# Revit family: ARKOSLIGHT_Alaska Trimless
name_source: partatom
category: Lighting Fixtures
units: mm (PartAtom-declared; Revit-internal decimal feet)

## family parameters
Cut with Voids When Loaded = No
Host = Face
Light Source = No
Part Type = Normal
Room Calculation Point = No
Round Connector Dimension = Use Diameter
Shared = No

## types (2) — shared parameters
ARKOSLIGHT_Apparent Load = 5 VA
ARKOSLIGHT_Beam Angle = 21.00°
ARKOSLIGHT_Body Color = ARKOSLIGHT_Black
ARKOSLIGHT_CRI = CRI>90
ARKOSLIGHT_Color = Black
ARKOSLIGHT_Dimming = No Dim / DALI
ARKOSLIGHT_Efficiency = 30%
ARKOSLIGHT_Fixture Type = CEILING RECESSED
ARKOSLIGHT_IP = 20
ARKOSLIGHT_Model = ALASKA TRIMLESS
ARKOSLIGHT_Series = ALASKA TRIMLESS
ARKOSLIGHT_Wattage = 5 W
Apparent Load = 5 VA
Manufacturer = ARKOSLIGHT
Model = ALASKA TRIMLESS
URL = https://www.arkoslight.com
zero-valued in all types: Default Elevation

## per-type parameters (varying)
| type | ARKOSLIGHT_CCT | ARKOSLIGHT_IES | ARKOSLIGHT_Luminous flux | ARKOSLIGHT_Reference | IES |
| A4010000N - ALASKA TRIMLESS 2700K N | 2700 K | A401-00-00 ALASKA TRIMLESS 2700K CRI90.ies | 475 lm | A4010000N | IES : A4010000N - ALASKA TRIMLESS 2700K N |
| A4010001N - ALASKA TRIMLESS 3000K N | 3000 K | A401-00-01 ALASKA TRIMLESS 3000K CRI90.ies | 500 lm | A4010001N | IES : A4010001N - ALASKA TRIMLESS 3000K N |

## geometry (parser evidence)
native form markers: Sweep x8
no freeform markers — native parametric forms only
